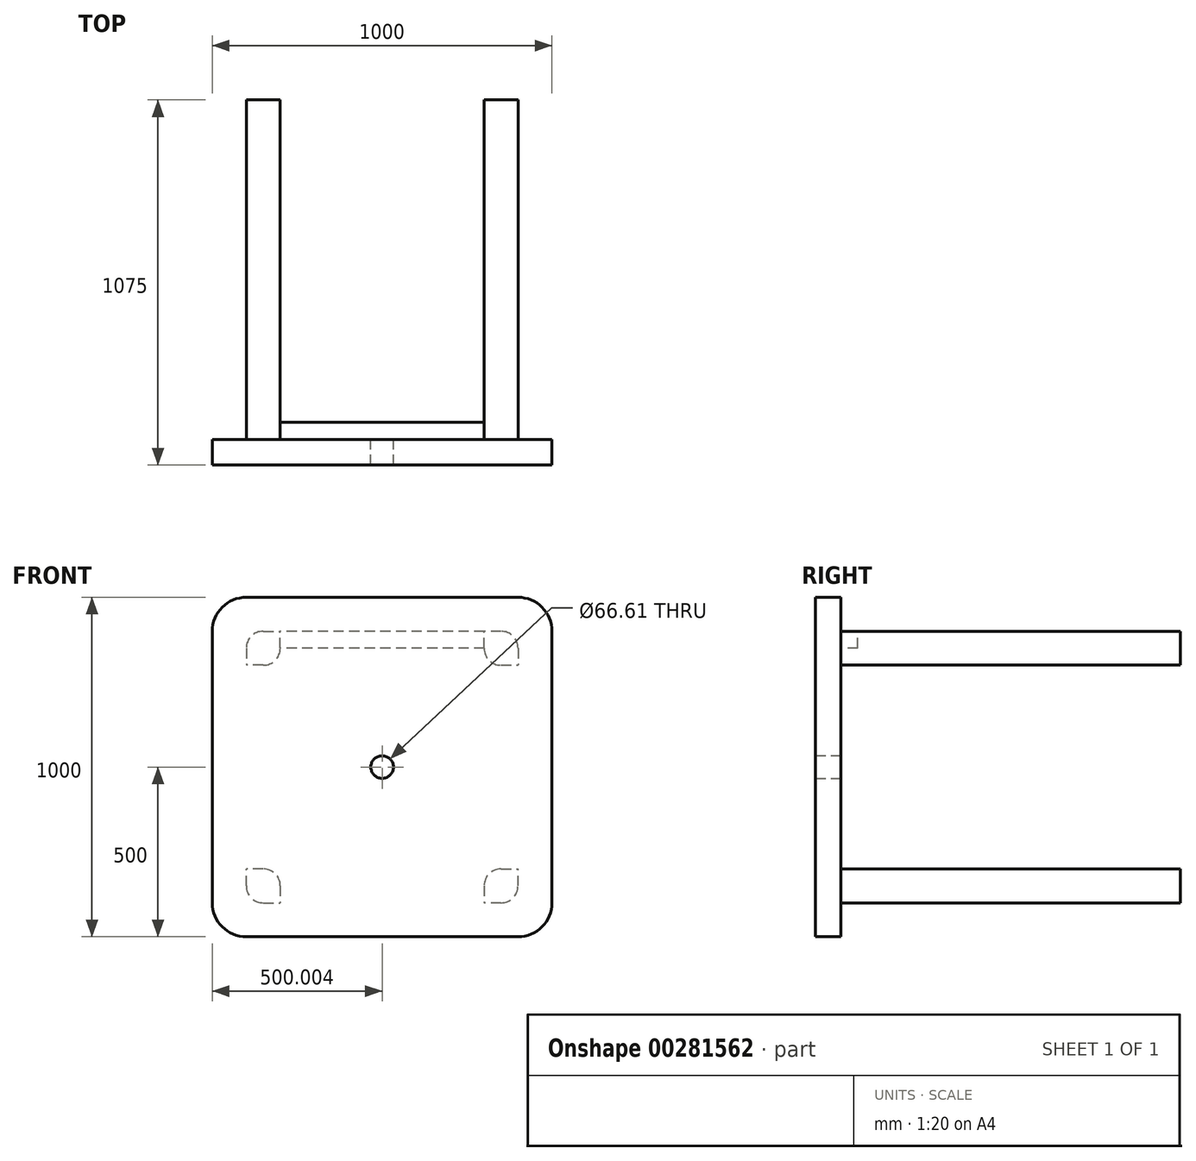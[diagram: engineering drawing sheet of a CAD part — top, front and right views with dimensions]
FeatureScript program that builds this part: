
annotation { "Feature Type Name" : "Feature", "Feature Type Description" : "" }
export const myFeature = defineFeature(function(context is Context, id is Id, definition is map)
    precondition{}
    {
        {
            var Q0;
            Q0=qCreatedBy(makeId("Front.planeOp"),FACE);
            var sketch = newSketch(context, id + "F0", { "sketchPlane" : qUnion([Q0])});
            skLineSegment(sketch, "E0.bottom", {"start": v(-303.8, 598) * mm, "end": v(496.2, 598) * mm});
            skLineSegment(sketch, "E0.top", {"start": v(-303.8, -402) * mm, "end": v(496.2, -402) * mm});
            skLineSegment(sketch, "E0.left", {"start": v(-403.8, 498) * mm, "end": v(-403.8, -302) * mm});
            skLineSegment(sketch, "E0.right", {"start": v(596.2, 498) * mm, "end": v(596.2, -302) * mm});
            skPoint(sketch, "E1.visualSharp", {"position": v(596.2, 598) * mm});
            skArc(sketch, "E1.filletArc", {"start": v(596.2, 498) * mm, "mid": v(566.9, 568.7) * mm, "end": v(496.2, 598) * mm});
            skPoint(sketch, "E2.visualSharp", {"position": v(-403.8, -402) * mm});
            skArc(sketch, "E2.filletArc", {"start": v(-403.8, -302) * mm, "mid": v(-374.52, -372.72) * mm, "end": v(-303.8, -402) * mm});
            skPoint(sketch, "E3.visualSharp", {"position": v(-403.8, 598) * mm});
            skArc(sketch, "E3.filletArc", {"start": v(-303.8, 598) * mm, "mid": v(-374.52, 568.7) * mm, "end": v(-403.8, 498) * mm});
            skPoint(sketch, "E4.visualSharp", {"position": v(596.2, -402) * mm});
            skArc(sketch, "E4.filletArc", {"start": v(496.2, -402) * mm, "mid": v(566.9, -372.72) * mm, "end": v(596.2, -302) * mm});
            skCircle(sketch, "E5", {"center": v(96.2, 98) * mm, "radius": 33.3 * mm});
            skSolve(sketch);
        }
        {
            var Q0;
            Q0=makeQuery(id+"F0.imprint","IMPRINT",FACE,{"disambiguationData":[TD([[makeQuery(id+"F0.imprint","IMPRINT",EDGE,{"derivedFrom":sQuery(id+"F0.wireOp",EDGE,"E0.bottom")}),-1.0]])]});
            extrude(context, id + "F1", {"entities" : qUnion([Q0]), "endBound" : BoundingType.SYMMETRIC, "depth" : 50 * mm});
        }
        {
            var Q0;
            Q0=makeQuery(id+"F1.opExtrude","CAP_FACE",FACE,{"disambiguationData":[OSD([sQuery(id+"F0.wireOp",EDGE,"E0.bottom"),sQuery(id+"F0.wireOp",EDGE,"E0.top"),sQuery(id+"F0.wireOp",EDGE,"E0.left"),sQuery(id+"F0.wireOp",EDGE,"E0.right")])],"isStart":true});
            var sketch = newSketch(context, id + "F2", { "sketchPlane" : qUnion([Q0])});
            skLineSegment(sketch, "E6.0", {"start": v(79.83, 42.92) * mm, "end": v(80.46, 42.3) * mm});
            skPoint(sketch, "E6.0.midPoint", {"position": v(80.15, 42.6) * mm});
            skLineSegment(sketch, "E7.bottom", {"start": v(-446.2, -302) * mm, "end": v(-396.2, -302) * mm});
            skLineSegment(sketch, "E7.left", {"start": v(-496.2, -252) * mm, "end": v(-496.2, -202) * mm});
            skLineSegment(sketch, "E8.bottom", {"start": v(-446.2, 498) * mm, "end": v(-396.2, 498) * mm});
            skLineSegment(sketch, "E8.left", {"start": v(-496.2, 448) * mm, "end": v(-496.2, 398) * mm});
            skLineSegment(sketch, "E9.bottom", {"start": v(253.8, 498) * mm, "end": v(203.8, 498) * mm});
            skLineSegment(sketch, "E9.left", {"start": v(303.8, 448) * mm, "end": v(303.8, 398) * mm});
            skLineSegment(sketch, "E10.bottom", {"start": v(253.8, -302) * mm, "end": v(203.8, -302) * mm});
            skLineSegment(sketch, "E10.left", {"start": v(303.8, -252) * mm, "end": v(303.8, -202) * mm});
            skPoint(sketch, "E11.visualSharp", {"position": v(-496.2, 498) * mm});
            skArc(sketch, "E11.filletArc", {"start": v(-446.2, 498) * mm, "mid": v(-481.55, 483.35) * mm, "end": v(-496.2, 448) * mm});
            skPoint(sketch, "E12.visualSharp", {"position": v(303.8, 498) * mm});
            skArc(sketch, "E12.filletArc", {"start": v(303.8, 448) * mm, "mid": v(289.16, 483.35) * mm, "end": v(253.8, 498) * mm});
            skPoint(sketch, "E13.visualSharp", {"position": v(-496.2, -302) * mm});
            skArc(sketch, "E13.filletArc", {"start": v(-496.2, -252) * mm, "mid": v(-481.55, -287.37) * mm, "end": v(-446.2, -302) * mm});
            skPoint(sketch, "E14.visualSharp", {"position": v(303.8, -302) * mm});
            skArc(sketch, "E14.filletArc", {"start": v(253.8, -302) * mm, "mid": v(289.16, -287.37) * mm, "end": v(303.8, -252) * mm});
            skLineSegment(sketch, "E15", {"start": v(-396.2, 498) * mm, "end": v(-496.2, 398) * mm});
            skLineSegment(sketch, "E16", {"start": v(203.8, 498) * mm, "end": v(303.8, 398) * mm});
            skLineSegment(sketch, "E17", {"start": v(-396.2, -302) * mm, "end": v(-496.2, -202) * mm});
            skLineSegment(sketch, "E18", {"start": v(203.8, -302) * mm, "end": v(303.8, -202) * mm});
            skLineSegment(sketch, "E19.MirrorCS", {"start": v(203.8, 448) * mm, "end": v(203.8, 498) * mm});
            skPoint(sketch, "E20.MirrorP", {"position": v(203.8, 398) * mm});
            skArc(sketch, "E21.MirrorCS", {"start": v(253.8, 398) * mm, "mid": v(218.45, 412.63) * mm, "end": v(203.8, 448) * mm});
            skLineSegment(sketch, "E22.MirrorCS", {"start": v(253.8, 398) * mm, "end": v(303.8, 398) * mm});
            skPoint(sketch, "E23.MirrorP", {"position": v(-396.2, 398) * mm});
            skArc(sketch, "E24.MirrorCS", {"start": v(-396.2, 448) * mm, "mid": v(-410.84, 412.63) * mm, "end": v(-446.2, 398) * mm});
            skLineSegment(sketch, "E25.MirrorCS", {"start": v(-396.2, 448) * mm, "end": v(-396.2, 498) * mm});
            skLineSegment(sketch, "E26.MirrorCS", {"start": v(-446.2, 398) * mm, "end": v(-496.2, 398) * mm});
            skArc(sketch, "E27.MirrorCS", {"start": v(-446.2, -202) * mm, "mid": v(-410.84, -216.65) * mm, "end": v(-396.2, -252) * mm});
            skLineSegment(sketch, "E28.MirrorCS", {"start": v(-396.2, -252) * mm, "end": v(-396.2, -302) * mm});
            skPoint(sketch, "E29.MirrorP", {"position": v(-396.2, -202) * mm});
            skLineSegment(sketch, "E30.MirrorCS", {"start": v(-446.2, -202) * mm, "end": v(-496.2, -202) * mm});
            skLineSegment(sketch, "E31.MirrorCS", {"start": v(203.8, -252) * mm, "end": v(203.8, -302) * mm});
            skLineSegment(sketch, "E32.MirrorCS", {"start": v(253.8, -202) * mm, "end": v(303.8, -202) * mm});
            skArc(sketch, "E33.MirrorCS", {"start": v(203.8, -252) * mm, "mid": v(218.45, -216.65) * mm, "end": v(253.8, -202) * mm});
            skPoint(sketch, "E34.MirrorP", {"position": v(203.8, -202) * mm});
            skSolve(sketch);
        }
        {
            var Q0;
            Q0=makeQuery(id+"F2.imprint","IMPRINT",FACE,{"disambiguationData":[TD([[makeQuery(id+"F2.imprint","IMPRINT",EDGE,{"derivedFrom":sQuery(id+"F2.wireOp",EDGE,"E8.bottom")}),-1.0]])]});
            var Q1;
            Q1=makeQuery(id+"F2.imprint","IMPRINT",FACE,{"disambiguationData":[TD([[makeQuery(id+"F2.imprint","IMPRINT",EDGE,{"derivedFrom":sQuery(id+"F2.wireOp",EDGE,"E9.bottom")}),1.0]])]});
            var Q2;
            Q2=makeQuery(id+"F2.imprint","IMPRINT",FACE,{"disambiguationData":[TD([[makeQuery(id+"F2.imprint","IMPRINT",EDGE,{"derivedFrom":sQuery(id+"F2.wireOp",EDGE,"E10.bottom")}),-1.0]])]});
            var Q3;
            Q3=makeQuery(id+"F2.imprint","IMPRINT",FACE,{"disambiguationData":[TD([[makeQuery(id+"F2.imprint","IMPRINT",EDGE,{"derivedFrom":sQuery(id+"F2.wireOp",EDGE,"E7.bottom")}),1.0]])]});
            var Q4;
            Q4=makeQuery(id+"F2.imprint","IMPRINT",FACE,{"disambiguationData":[TD([[makeQuery(id+"F2.imprint","IMPRINT",EDGE,{"derivedFrom":sQuery(id+"F2.wireOp",EDGE,"E18")}),1.0]])]});
            var Q5;
            Q5=makeQuery(id+"F2.imprint","IMPRINT",FACE,{"disambiguationData":[TD([[makeQuery(id+"F2.imprint","IMPRINT",EDGE,{"derivedFrom":sQuery(id+"F2.wireOp",EDGE,"E17")}),-1.0]])]});
            var Q6;
            Q6=makeQuery(id+"F2.imprint","IMPRINT",FACE,{"disambiguationData":[TD([[makeQuery(id+"F2.imprint","IMPRINT",EDGE,{"derivedFrom":sQuery(id+"F2.wireOp",EDGE,"E15")}),1.0]])]});
            var Q7;
            Q7=makeQuery(id+"F2.imprint","IMPRINT",FACE,{"disambiguationData":[TD([[makeQuery(id+"F2.imprint","IMPRINT",EDGE,{"derivedFrom":sQuery(id+"F2.wireOp",EDGE,"E16")}),-1.0]])]});
            extrude(context, id + "F3", {"entities" : qUnion([Q0, Q1, Q2, Q3, Q4, Q5, Q6, Q7]), "depth" : 1000 * mm});
        }
        {
            var Q0;
            Q0 = qSketchRegion(id + "F0", true);
            extrude(context, id + "F4", {"entities" : qUnion([Q0]), "operationType" : NewBodyOperationType.ADD, "depth" : 50 * mm});
        }
        {
            var Q0;
            Q0=makeQuery(id+"F3.opExtrude","SWEPT_FACE",FACE,{"disambiguationData":[OSD([sQuery(id+"F2.wireOp",EDGE,"E19.MirrorCS")])]});
            var sketch = newSketch(context, id + "F5", { "sketchPlane" : qUnion([Q0])});
            skLineSegment(sketch, "E35", {"start": v(25, 448) * mm, "end": v(75, 448) * mm});
            skLineSegment(sketch, "E36", {"start": v(75, 448) * mm, "end": v(75, 498) * mm});
            skLineSegment(sketch, "E37", {"start": v(75, 498) * mm, "end": v(25, 498) * mm});
            skLineSegment(sketch, "E38", {"start": v(25, 498) * mm, "end": v(25, 448) * mm});
            skSolve(sketch);
        }
        {
            var Q0;
            Q0=makeQuery(id+"F5.imprint","IMPRINT",FACE,{"disambiguationData":[TD([[makeQuery(id+"F5.imprint","IMPRINT",EDGE,{"derivedFrom":sQuery(id+"F5.wireOp",EDGE,"E35")}),-1.0]])]});
            extrude(context, id + "F6", {"entities" : qUnion([Q0]), "depth" : 600.7 * mm});
        }
    });
